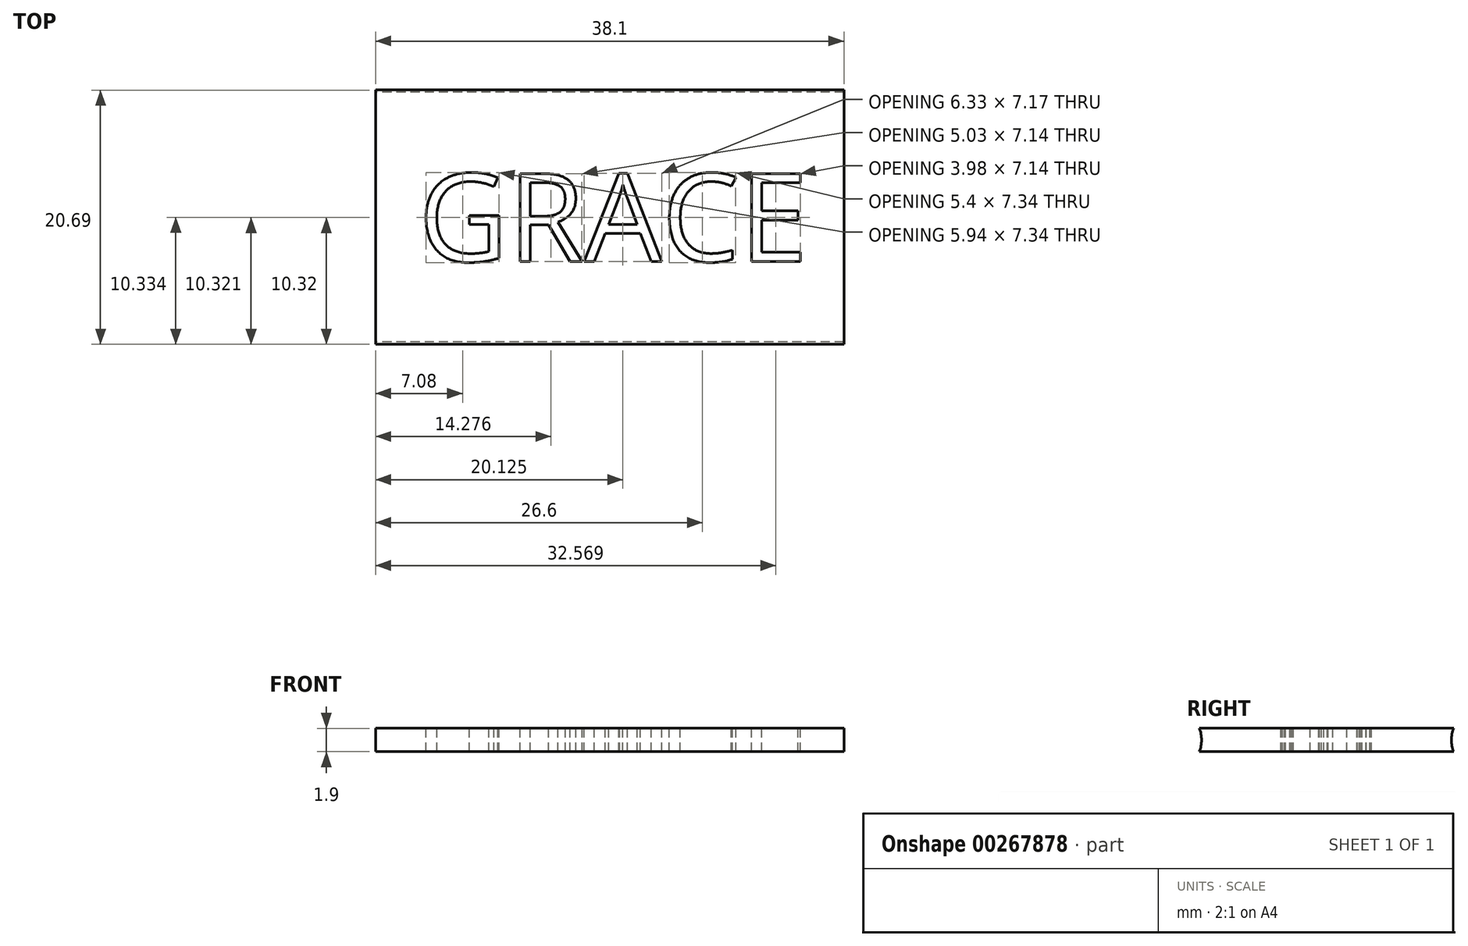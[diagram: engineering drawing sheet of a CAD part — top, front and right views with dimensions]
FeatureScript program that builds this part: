
annotation { "Feature Type Name" : "Feature", "Feature Type Description" : "" }
export const myFeature = defineFeature(function(context is Context, id is Id, definition is map)
    precondition{}
    {
        {
            var Q0;
            Q0=qCreatedBy(makeId("Right.planeOp"),FACE);
            var sketch = newSketch(context, id + "F0", { "sketchPlane" : qUnion([Q0])});
            skLineSegment(sketch, "E0", {"start": v(-15.28, 0) * mm, "end": v(10.12, 0) * mm});
            skArc(sketch, "E1", {"start": v(7.76, 0.95) * mm, "mid": v(7.58, 0) * mm, "end": v(7.76, -0.95) * mm});
            skArc(sketch, "E2", {"start": v(-12.93, -0.95) * mm, "mid": v(-12.74, 0) * mm, "end": v(-12.93, 0.95) * mm});
            skPoint(sketch, "E3", {"position": v(0, 0.95) * mm});
            skPoint(sketch, "E4", {"position": v(0, -0.95) * mm});
            skLineSegment(sketch, "E5.bottom", {"start": v(0, 0.95) * mm, "end": v(7.76, 0.95) * mm});
            skLineSegment(sketch, "E5.top", {"start": v(0, -0.95) * mm, "end": v(7.76, -0.95) * mm});
            skLineSegment(sketch, "E5.left", {"start": v(0, 0.95) * mm, "end": v(0, -0.95) * mm});
            skLineSegment(sketch, "E5.right", {"start": v(7.76, 0.95) * mm, "end": v(7.76, -0.95) * mm});
            skLineSegment(sketch, "E6.bottom", {"start": v(0, 0.95) * mm, "end": v(-12.93, 0.95) * mm});
            skLineSegment(sketch, "E6.top", {"start": v(0, -0.95) * mm, "end": v(-12.93, -0.95) * mm});
            skLineSegment(sketch, "E6.right", {"start": v(-12.93, 0.95) * mm, "end": v(-12.93, -0.95) * mm});
            skPoint(sketch, "E7.orphan", {"position": v(10.12, 2.54) * mm});
            skSolve(sketch);
        }
        {
            var Q0;
            {var subQ5=sQuery(id+"F0.wireOp",EDGE,"E6.top");Q0=makeQuery(id+"F0.imprint","IMPRINT",FACE,{"disambiguationData":[TD([[makeQuery(id+"F0.imprint","IMPRINT",EDGE,{"derivedFrom":subQ5}),-1.0]])]});}
            var Q1;
            {var subQ5=sQuery(id+"F0.wireOp",EDGE,"E6.bottom");Q1=makeQuery(id+"F0.imprint","IMPRINT",FACE,{"disambiguationData":[TD([[makeQuery(id+"F0.imprint","IMPRINT",EDGE,{"derivedFrom":subQ5}),1.0]])]});}
            var Q2;
            {var subQ5=sQuery(id+"F0.wireOp",EDGE,"E5.top");Q2=makeQuery(id+"F0.imprint","IMPRINT",FACE,{"disambiguationData":[TD([[makeQuery(id+"F0.imprint","IMPRINT",EDGE,{"derivedFrom":subQ5}),1.0]])]});}
            var Q3;
            {var subQ5=sQuery(id+"F0.wireOp",EDGE,"E5.bottom");Q3=makeQuery(id+"F0.imprint","IMPRINT",FACE,{"disambiguationData":[TD([[makeQuery(id+"F0.imprint","IMPRINT",EDGE,{"derivedFrom":subQ5}),-1.0]])]});}
            extrude(context, id + "F1", {"entities" : qUnion([Q0, Q1, Q2, Q3]), "depth" : 38.1 * mm});
        }
        {
            var Q0;
            Q0=makeQuery(id+"F1.opExtrude","SWEPT_FACE",FACE,{"disambiguationData":[OSD([sQuery(id+"F0.wireOp",EDGE,"E5.bottom"),sQuery(id+"F0.wireOp",EDGE,"E6.bottom")])]});
            var sketch = newSketch(context, id + "F2", { "sketchPlane" : qUnion([Q0])});
            skText(sketch, "E8", { "text": "GRACE \n", "fontName": "OpenSans-Regular.ttf"});
            const initialGuessF2  = {"E8": [0.0035, -0.00618, 1, 0, 0.0072]};
            skSetInitialGuess(sketch, initialGuessF2);
            skSolve(sketch);
        }
        {
            var Q0;
            Q0 = qSketchRegion(id + "F2", true);
            extrude(context, id + "F3", {"entities" : qUnion([Q0]), "operationType" : NewBodyOperationType.REMOVE, "oppositeDirection" : true, "depth" : 25.4 * mm});
        }
    });
